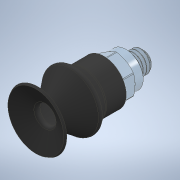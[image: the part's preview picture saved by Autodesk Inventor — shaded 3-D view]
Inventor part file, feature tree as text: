
AUTODESK INVENTOR PART (.ipt)
format: ipt  version: 2022 (Build 260153000, 153)  size: 480,768 bytes
history: native  units: in
note: dims shown in document units (in); Inventor stores cm internally (conversion verified against a paired STEP export)
features: revolve x2, other x1
ambient origin geometry x8: Origin, YZ Plane, XZ Plane, XY Plane, X Axis, Y Axis, Z Axis, Center Point
bodies: Solid1 (feature_tree), Solid2 (feature_tree), Solid3 (feature_tree)
feature tree (3):
  revolve  "Revolve1"  [1 undecoded]
  other  "Boss-Extrude3"
  revolve  "Revolve3"  [1 undecoded]
note: 2 required parameter values undecoded (feature->parameter linkage not recoverable at this tier; creation-order binding heuristic only, values carry confidence <= 0.55)
